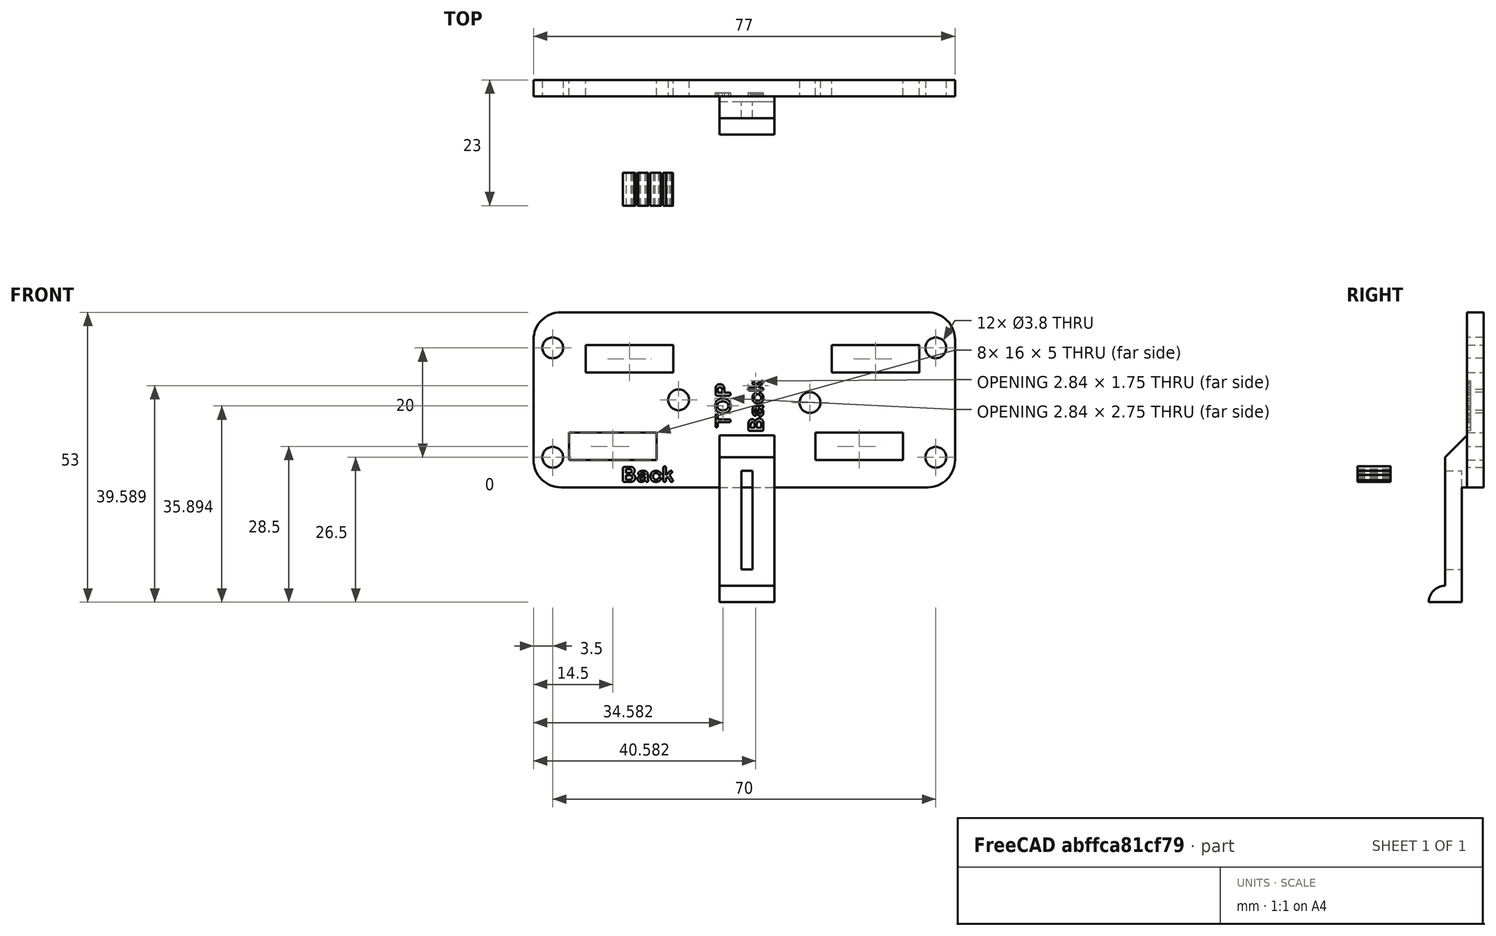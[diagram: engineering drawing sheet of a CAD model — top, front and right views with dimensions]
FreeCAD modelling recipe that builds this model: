
FCSTD DOCUMENT  (FreeCAD 0.16R6712 (Git))
Label: ParkingNozzleBackPlateRight
License: All rights reserved
LicenseURL: http://en.wikipedia.org/wiki/All_rights_reserved
objects: Part::Cylinder×14, Part::MultiFuse×10, Part::Box×9, Part::Cut×9, Part::Feature×4, Part::Part2DObjectPython×2, Part::Extrusion×1
note: 49 computed .brp shape members not serialized (recipe doc carries the construction recipe); baked Part::Feature solids carry a one-line shape summary decoded from their .brp

FEATURE [Part::Part2DObjectPython] ShapeString002  # Draft 2D object (typed FeaturePython)
  FontFile = <path>
  Size = 3
  String = TOP
  Tracking = 4
FEATURE [Part::Feature] Extrude001002001  label="Extrude001003"
  Placement = pos=(18,0,11) rot=(0,-1,0;1.5708rad)
  shape: bbox 2.835 x 6 x 7.877 mm, 76 faces, 3 solids (baked)
FEATURE [Part::Part2DObjectPython] ShapeString003  # Draft 2D object (typed FeaturePython)
  FontFile = <path>
  Size = 3
  String = Back
  Tracking = 4
FEATURE [Part::Extrusion] Extrude001002002
  Base = -> ShapeString003
  Dir = (0,0,6)
  Placement = pos=(0,0,0) rot=(1,0,0;1.5708rad)
  Solid = false
FEATURE [Part::Feature] Extrude001002002001  label="Extrude001002003"
  Placement = pos=(24,0,10) rot=(0,-1,0;1.5708rad)
  shape: bbox 2.835 x 6 x 9.142 mm, 140 faces, 4 solids (baked)
FEATURE [Part::Box] Box035  label="Würfel034"
  Height = 32
  Length = 77
  Placement = pos=(-16,14,-1) rot=(0,0,1;0rad)
  Width = 3
FEATURE [Part::MultiFuse] Fusion  label="Label"
  Placement = pos=(2,14.6,-1) rot=(0,0,1;0rad)
  Shapes = -> [Extrude001002002001,Extrude001002001]
FEATURE [Part::Cut] Cut
  Base = -> Box035
  Tool = -> Fusion
FEATURE [Part::Box] Box  label="Würfel"
  Height = 21
  Length = 10
  Placement = pos=(0,0,-2) rot=(0,0,1;0rad)
  Width = 3
FEATURE [Part::Feature] Cylinder040  label="Zylinder031"
  Placement = pos=(0,0,-2) rot=(1,0,0;1.5708rad)
  shape: bbox 10 x 6 x 3 mm, 4 faces (baked)
FEATURE [Part::MultiFuse] Fusion026006
  Placement = pos=(18,10,-20) rot=(0,0,1;0rad)
  Shapes = -> [Box,Cylinder040]
FEATURE [Part::Cylinder] Cylinder051  label="Zylinder042"
  Angle = 90
  Height = 40
  Placement = pos=(33,25,29) rot=(1,0,0;1.5708rad)
  Radius = 8
FEATURE [Part::Cylinder] Cylinder052  label="Zylinder043"
  Angle = 90
  Height = 40
  Placement = pos=(33,25,29) rot=(1,0,0;1.5708rad)
  Radius = 5
FEATURE [Part::Cut] Cut011004004
  Base = -> Cylinder051
  Placement = pos=(18,0,-7) rot=(0,-1,0;1.5708rad)
  Tool = -> Cylinder052
FEATURE [Part::Cylinder] Cylinder053  label="Zylinder044"
  Angle = 90
  Height = 40
  Placement = pos=(33,25,29) rot=(1,0,0;1.5708rad)
  Radius = 8
FEATURE [Part::Cylinder] Cylinder054  label="Zylinder045"
  Angle = 90
  Height = 40
  Placement = pos=(33,25,29) rot=(1,0,0;1.5708rad)
  Radius = 5
FEATURE [Part::Cut] Cut011004005
  Base = -> Cylinder053
  Placement = pos=(22,0,33) rot=(0,1,0;3.14159rad)
  Tool = -> Cylinder054
FEATURE [Part::Cylinder] Cylinder055  label="Zylinder046"
  Angle = 90
  Height = 40
  Placement = pos=(33,25,29) rot=(1,0,0;1.5708rad)
  Radius = 8
FEATURE [Part::Cylinder] Cylinder056  label="Zylinder047"
  Angle = 90
  Height = 40
  Placement = pos=(33,25,29) rot=(1,0,0;1.5708rad)
  Radius = 5
FEATURE [Part::Cut] Cut011004006
  Base = -> Cylinder055
  Placement = pos=(23,0,-3) rot=(0,0,1;0rad)
  Tool = -> Cylinder056
FEATURE [Part::Cylinder] Cylinder059  label="Zylinder050"
  Angle = 90
  Height = 40
  Placement = pos=(33,25,29) rot=(1,0,0;1.5708rad)
  Radius = 8
FEATURE [Part::Cylinder] Cylinder060  label="Zylinder051"
  Angle = 90
  Height = 40
  Placement = pos=(33,25,29) rot=(1,0,0;1.5708rad)
  Radius = 5
FEATURE [Part::Cut] Cut011004008
  Base = -> Cylinder059
  Placement = pos=(27,0,37) rot=(0,1,0;1.5708rad)
  Tool = -> Cylinder060
FEATURE [Part::MultiFuse] Fusion026012  label="RoundEdges"
  Shapes = -> [Cut011004008,Cut011004006,Cut011004004,Cut011004005]
FEATURE [Part::Box] Box037  label="Würfel036"
  Height = 10
  Length = 10
  Width = 4
FEATURE [Part::Box] Box038  label="Würfel037"
  Height = 10
  Length = 10
  Placement = pos=(0,-5,9) rot=(-1,0,0;0.785398rad)
  Width = 6
FEATURE [Part::Cut] Cut011004009
  Base = -> Box037
  Placement = pos=(18,10,-1) rot=(0,0,1;0rad)
  Tool = -> Box038
FEATURE [Part::Box] Box041  label="Würfel040"
  Height = 18
  Length = 2
  Placement = pos=(22,-1,-16) rot=(0,0,1;0rad)
  Width = 14
FEATURE [Part::MultiFuse] Fusion026014
  Shapes = -> [Fusion026006,Cut011004009]
FEATURE [Part::Cut] Cut011004012  label="DecuplerRight"
  Base = -> Fusion026014
  Tool = -> Box041
FEATURE [Part::Cylinder] Cylinder034  label="Zylinder025"
  Angle = 360
  Height = 26
  Placement = pos=(-13,16,4.5) rot=(1,0,0;1.5708rad)
  Radius = 1.9
FEATURE [Part::Cylinder] Cylinder035  label="Zylinder026"
  Angle = 360
  Height = 26
  Placement = pos=(-13,16,24.5) rot=(1,0,0;1.5708rad)
  Radius = 1.9
FEATURE [Part::Cylinder] Cylinder036  label="Zylinder027"
  Angle = 360
  Height = 26
  Placement = pos=(10.5,16,15) rot=(1,0,0;1.5708rad)
  Radius = 1.9
FEATURE [Part::MultiFuse] Fusion026003
  Placement = pos=(0.5,0,0) rot=(0,0,1;0rad)
  Shapes = -> [Cylinder034,Cylinder035]
FEATURE [Part::Cylinder] Cylinder037  label="Zylinder028"
  Angle = 360
  Height = 26
  Placement = pos=(-13,16,4.5) rot=(1,0,0;1.5708rad)
  Radius = 1.9
FEATURE [Part::Cylinder] Cylinder038  label="Zylinder029"
  Angle = 360
  Height = 26
  Placement = pos=(-13,16,24.5) rot=(1,0,0;1.5708rad)
  Radius = 1.9
FEATURE [Part::MultiFuse] Fusion026004
  Placement = pos=(70.5,0,0) rot=(0,0,1;0rad)
  Shapes = -> [Cylinder037,Cylinder038]
FEATURE [Part::Cylinder] Cylinder039  label="Zylinder030"
  Angle = 360
  Height = 26
  Placement = pos=(34.5,16,14.5) rot=(1,0,0;1.5708rad)
  Radius = 1.9
FEATURE [Part::MultiFuse] Fusion026005  label="Bohrung"
  Placement = pos=(0,3,0) rot=(0,0,1;0rad)
  Shapes = -> [Cylinder036,Fusion026003,Fusion026004,Cylinder039]
FEATURE [Part::MultiFuse] Fusion026015
  Shapes = -> [Fusion026012,Fusion026005]
FEATURE [Part::Cut] Cut011004013  label="BasePlate"
  Base = -> Cut
  Tool = -> Fusion026015
FEATURE [Part::MultiFuse] Fusion026016  label="DecupplingPlateRight"
  Shapes = -> [Cut011004012,Cut011004013]
FEATURE [Part::Box] Box034  label="Würfel033"
  Height = 5
  Length = 16
  Placement = pos=(-9.5,-18,4) rot=(0,0,1;0rad)
  Width = 10
FEATURE [Part::Box] Box043  label="Würfel042"
  Height = 5
  Length = 16
  Placement = pos=(35.5,-18,4) rot=(0,0,1;0rad)
  Width = 10
FEATURE [Part::Box] Box044  label="Würfel043"
  Height = 5
  Length = 16
  Placement = pos=(-6.5,-18,20) rot=(0,0,1;0rad)
  Width = 10
FEATURE [Part::Box] Box045  label="Würfel044"
  Height = 5
  Length = 16
  Placement = pos=(38.5,-18,20) rot=(0,0,1;0rad)
  Width = 10
FEATURE [Part::MultiFuse] Fusion026017  label="SripperHoles"
  Placement = pos=(0,26,0) rot=(0,0,1;0rad)
  Shapes = -> [Box034,Box045,Box043,Box044]
FEATURE [Part::Cut] Cut011004014  label="BackPlateRight"
  Base = -> Fusion026016
  Tool = -> Fusion026017
FEATURE [Part::Feature] Cut011004014001  label="BackPlateRight_export"
  shape: bbox 77 x 10 x 53 mm, 258 faces (baked)
note: 2 file-system paths scrubbed to <path> (originals preserved in the JSON sidecar)
